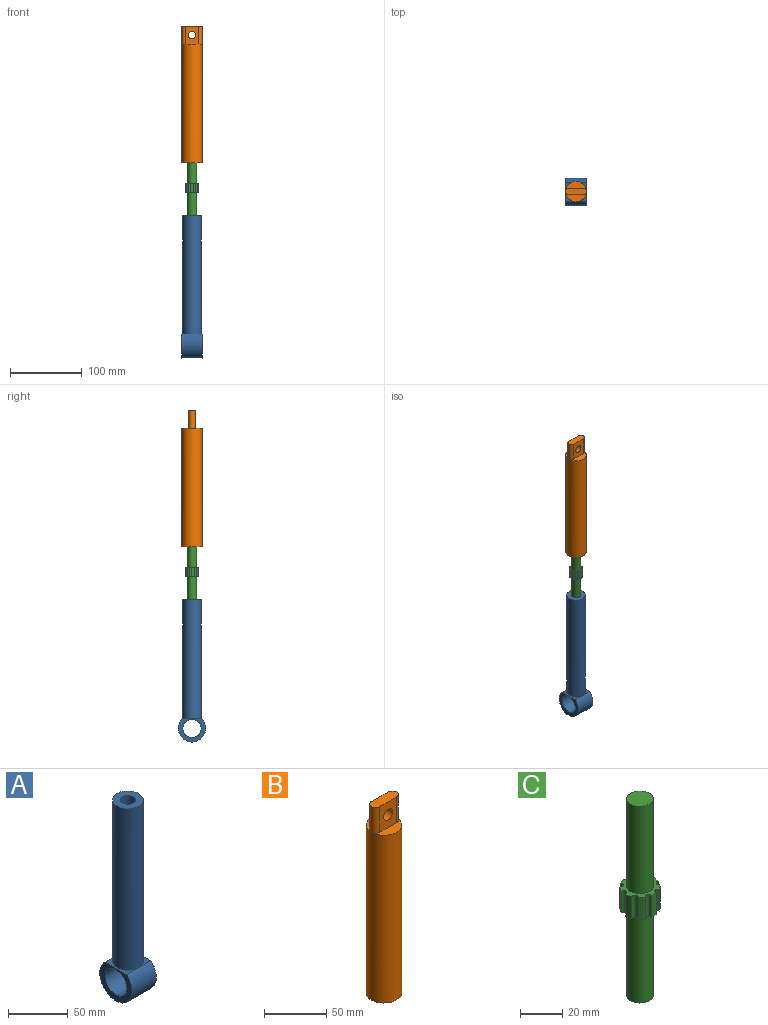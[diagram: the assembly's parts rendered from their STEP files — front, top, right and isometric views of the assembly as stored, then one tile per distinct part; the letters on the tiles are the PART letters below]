
ASSEMBLY  parts=3 mates=2
PART A: 10 faces, bbox 28.6x38.1x198.2 mm
  f0: plane 25.63x14.29mm, normal (0,0,1), area 108.3mm2, adj f3,f5,f6
  f1: plane 25.63x14.29mm, normal (0,0,1), area 108.3mm2, adj f3,f4,f6
  f2: cylinder r=12.7mm len=28.58mm, axis (-1,0,0), area 2280.2mm2, adj f4,f5
  f3: cylinder r=19.05mm len=38.1mm, axis (-1,0,0), area 2617.1mm2, adj f0,f1,f4,f5
  f4: plane 38.1x33.15mm, normal (-1,0,0), area 546.3mm2, adj f1,f2,f3
  f5: plane 38.1x33.15mm, normal (1,0,0), area 546.3mm2, adj f0,f2,f3
  f6: cylinder r=12.81mm len=165.1mm, axis (0,0,-1), area 13291.5mm2, adj f0,f1,f7
  f7: plane 25.63x25.63mm, normal (0,0,1), area 389.1mm2, adj f6,f8
  f8: cylinder r=6.35mm len=50.8mm, axis (0,0,1), area 2026.8mm2, adj f7,f9
  f9: plane 12.7x12.7mm, normal (0,0,1), area 126.7mm2, adj f8
PART B: 12 faces, bbox 28.6x28.6x190.5 mm
  f0: cylinder r=4.76mm len=25.4mm, axis (0,0,-1), area 380mm2, adj f1,f3,f4,f6,f9
  f1: plane 25.4x19.05mm, normal (0,1,0), area 402mm2, adj f0,f2,f4,f5,f6
  f2: cylinder r=4.76mm len=25.4mm, axis (0,0,-1), area 380mm2, adj f1,f3,f4,f6,f9
  f3: plane 25.4x19.05mm, normal (0,-1,0), area 402mm2, adj f0,f2,f4,f5,f9
  f4: plane 28.58x9.53mm, normal (0,0,1), area 252.7mm2, adj f0,f1,f2,f3
  f5: cylinder r=5.1mm len=10.21mm, axis (0,-1,0), area 305.4mm2, adj f1,f3
  f6: plane 28.58x14.29mm, normal (0,0,1), area 194.3mm2, adj f0,f1,f2,f7
  f7: cylinder r=14.29mm len=165.1mm, axis (0,0,1), area 14821.2mm2, adj f6,f8,f9
  f8: plane 28.58x28.58mm, normal (0,0,-1), area 514.6mm2, adj f7,f10
  f9: plane 28.58x14.29mm, normal (0,0,1), area 194.3mm2, adj f0,f2,f3,f7
  f10: cylinder r=6.35mm len=50.8mm, axis (0,0,-1), area 2026.8mm2, adj f8,f11
  f11: plane 12.7x12.7mm, normal (0,0,-1), area 126.7mm2, adj f10
PART C: 24 faces, bbox 19.1x18.9x114.3 mm
  f0: cylinder r=1.59mm len=12.7mm, axis (0,0,-1), area 60mm2, adj f1,f17,f18,f19
  f1: cylinder r=9.53mm len=12.7mm, axis (0,0,-1), area 44.1mm2, adj f0,f2,f18,f19
  f2: cylinder r=1.59mm len=12.7mm, axis (0,0,-1), area 60mm2, adj f1,f3,f18,f19
  f3: cylinder r=9.53mm len=12.7mm, axis (0,0,-1), area 44.1mm2, adj f2,f4,f18,f19
  f4: cylinder r=1.59mm len=12.7mm, axis (0,0,-1), area 60mm2, adj f3,f5,f18,f19
  f5: cylinder r=9.53mm len=12.7mm, axis (0,0,-1), area 44.1mm2, adj f4,f6,f18,f19
  f6: cylinder r=1.59mm len=12.7mm, axis (0,0,-1), area 60mm2, adj f5,f7,f18,f19
  f7: cylinder r=9.53mm len=12.7mm, axis (0,0,-1), area 44.1mm2, adj f6,f8,f18,f19
  f8: cylinder r=1.59mm len=12.7mm, axis (0,0,-1), area 60mm2, adj f7,f9,f18,f19
  f9: cylinder r=9.53mm len=12.7mm, axis (0,0,-1), area 44.1mm2, adj f8,f10,f18,f19
  f10: cylinder r=1.59mm len=12.7mm, axis (0,0,-1), area 60mm2, adj f9,f11,f18,f19
  f11: cylinder r=9.53mm len=12.7mm, axis (0,0,-1), area 44.1mm2, adj f10,f12,f18,f19
  f12: cylinder r=1.59mm len=12.7mm, axis (0,0,-1), area 60mm2, adj f11,f13,f18,f19
  f13: cylinder r=9.53mm len=12.7mm, axis (0,0,-1), area 44.1mm2, adj f12,f14,f18,f19
  f14: cylinder r=1.59mm len=12.7mm, axis (0,0,-1), area 60mm2, adj f13,f15,f18,f19
  f15: cylinder r=9.53mm len=12.7mm, axis (0,0,-1), area 44.1mm2, adj f14,f16,f18,f19
  f16: cylinder r=1.59mm len=12.7mm, axis (0,0,-1), area 60mm2, adj f15,f17,f18,f19
  f17: cylinder r=9.53mm len=12.7mm, axis (0,0,-1), area 44.1mm2, adj f0,f16,f18,f19
  f18: plane 19.05x18.92mm, normal (0,0,1), area 124mm2, adj f0,f1,f2,f3,f4,f5,f6,f7
  f19: plane 19.05x18.92mm, normal (0,0,-1), area 124mm2, adj f0,f1,f2,f3,f4,f5,f6,f7
  f20: cylinder r=6.35mm len=50.8mm, axis (0,0,-1), area 2026.8mm2, adj f18,f21
  f21: plane 12.7x12.7mm, normal (0,0,1), area 126.7mm2, adj f20
  f22: cylinder r=6.35mm len=50.8mm, axis (0,0,1), area 2026.8mm2, adj f19,f23
  f23: plane 12.7x12.7mm, normal (0,0,-1), area 126.7mm2, adj f22
PLACE A t=(40.77,-18.52,-279.42)mm
PLACE B t=(55.06,-18.52,139.36)mm
PLACE C t=(55.06,-18.52,-67.49)mm
MATE cylindrical A.f6 <-> C.f22  axis (0,0,-1) through (55.06,-18.52,-100.22)mm
MATE cylindrical C.f20 <-> B.f7  axis (0,0,-1) through (55.06,-18.52,-29.39)mm
